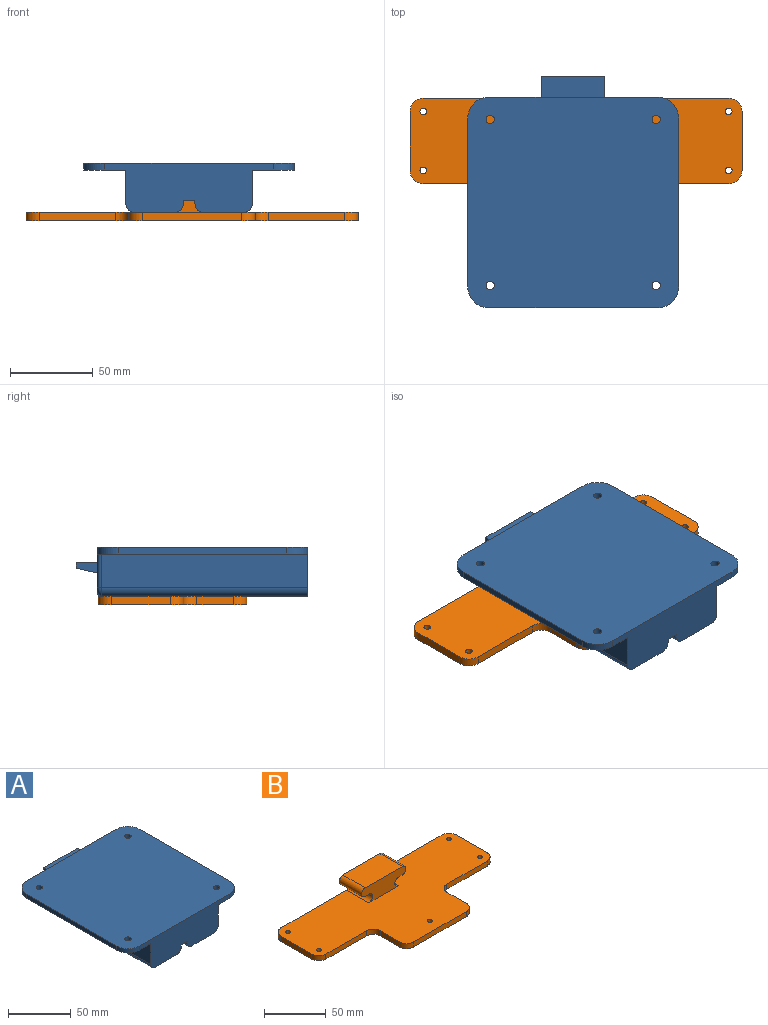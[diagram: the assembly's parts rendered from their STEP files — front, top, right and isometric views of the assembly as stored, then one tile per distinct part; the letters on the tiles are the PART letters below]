
ASSEMBLY  parts=2 mates=1
PART A: 55 faces, bbox 127x139.7x29.8 mm
  f0: plane 38.1x25.4mm, normal (0,0,-1), area 967.7mm2, adj f3,f27,f29,f33
  f1: plane 124.46x24.44mm, normal (0,0,-1), area 2850.8mm2, adj f2,f3,f9,f40,f42,f46
  f2: plane 101.6x29.4mm, normal (0,-1,0), area 2270.7mm2, adj f1,f10,f11,f12,f13,f15,f17,f23
  f3: plane 51.31x25.4mm, normal (0,1,0), area 840.4mm2, adj f0,f1,f4,f5,f6,f7,f8,f9
  f4: cylinder r=3.98mm len=22.86mm, axis (0,1,0), area 285.8mm2, adj f3,f5,f11,f51
  f5: plane 22.86x4.23mm, normal (0,0,1), area 96.8mm2, adj f3,f4,f6,f50
  f6: cylinder r=4.49mm len=22.86mm, axis (0,1,0), area 322.3mm2, adj f3,f5,f30,f49
  f7: cylinder r=4.49mm len=22.86mm, axis (0,1,0), area 322.3mm2, adj f3,f8,f26,f43
  f8: plane 22.86x4.23mm, normal (0,0,1), area 96.8mm2, adj f3,f7,f9,f44
  f9: cylinder r=3.98mm len=22.86mm, axis (0,1,0), area 285.8mm2, adj f1,f3,f8,f45
  f10: plane 124.46x20.32mm, normal (-1,0,0), area 2529mm2, adj f2,f17,f41,f54
  f11: plane 124.46x24.44mm, normal (0,0,-1), area 2850.8mm2, adj f2,f3,f4,f39,f41,f52
  f12: plane 124.46x20.32mm, normal (1,0,0), area 2529mm2, adj f2,f13,f42,f48
  f13: plane 127x27.94mm, normal (0,0,-1), area 3118.7mm2, adj f2,f12,f14,f18,f21,f22,f36,f38
  f14: plane 101.6x4mm, normal (1,0,0), area 406.4mm2, adj f13,f15,f36,f38
  f15: plane 127x127mm, normal (0,0,1), area 15912mm2, adj f2,f14,f16,f18,f19,f20,f21,f22
  f16: plane 101.6x4mm, normal (-1,0,0), area 406.4mm2, adj f15,f17,f35,f37
  f17: plane 127x27.94mm, normal (0,0,-1), area 3118.7mm2, adj f2,f10,f16,f18,f19,f20,f35,f37
  f18: plane 101.6x26.86mm, normal (0,1,0), area 937.4mm2, adj f13,f15,f17,f26,f30,f31,f35,f36
  f19: cylinder r=2.5mm len=5mm, axis (0,0,1), area 62.8mm2, adj f15,f17
  f20: cylinder r=2.5mm len=5mm, axis (0,0,1), area 62.8mm2, adj f15,f17
  f21: cylinder r=2.5mm len=5mm, axis (0,0,1), area 62.8mm2, adj f13,f15
  f22: cylinder r=2.5mm len=5mm, axis (0,0,1), area 62.8mm2, adj f13,f15
  f23: plane 101.6x1.92mm, normal (1,0,0), area 195.1mm2, adj f2,f3,f25,f39
  f24: plane 101.6x1.92mm, normal (-1,0,0), area 195.1mm2, adj f2,f3,f25,f40
  f25: plane 101.6x7mm, normal (0,0,-1), area 711.2mm2, adj f2,f3,f23,f24
  f26: plane 25.4x8.47mm, normal (-1,0,0), area 213.7mm2, adj f3,f7,f18,f31,f43
  f27: plane 38.1x6.21mm, normal (1,0,0), area 140.2mm2, adj f0,f3,f28,f32,f33,f34
  f28: plane 38.1x38.1mm, normal (0,0,1), area 1451.6mm2, adj f3,f27,f29,f32
  f29: plane 38.1x6.21mm, normal (-1,0,0), area 140.2mm2, adj f0,f3,f28,f32,f33,f34
  f30: plane 25.4x8.47mm, normal (1,0,0), area 213.7mm2, adj f3,f6,f18,f31,f49
  f31: plane 42.33x25.4mm, normal (0,0,-1), area 1075.3mm2, adj f3,f18,f26,f30
  f32: plane 38.1x3.18mm, normal (0,1,0), area 121mm2, adj f27,f28,f29,f34
  f33: plane 38.1x3.03mm, normal (0,-1,0), area 115.6mm2, adj f0,f27,f29,f34
  f34: plane 38.1x12.7mm, normal (0,0.23,-0.97), area 497.5mm2, adj f27,f29,f32,f33
  f35: cylinder r=12.7mm len=12.7mm, axis (0,0,-1), area 79.8mm2, adj f15,f16,f17,f18
  f36: cylinder r=12.7mm len=12.7mm, axis (0,0,1), area 79.8mm2, adj f13,f14,f15,f18
  f37: cylinder r=12.7mm len=12.7mm, axis (0,0,1), area 79.8mm2, adj f2,f15,f16,f17
  f38: cylinder r=12.7mm len=12.7mm, axis (0,0,-1), area 79.8mm2, adj f2,f13,f14,f15
  f39: cylinder r=5.08mm len=101.6mm, axis (0,1,0), area 810.7mm2, adj f2,f3,f11,f23
  f40: cylinder r=5.08mm len=101.6mm, axis (0,-1,0), area 810.7mm2, adj f1,f2,f3,f24
  f41: cylinder r=5.08mm len=124.46mm, axis (0,-1,0), area 993.1mm2, adj f2,f10,f11,f53
  f42: cylinder r=5.08mm len=124.46mm, axis (0,1,0), area 993.1mm2, adj f1,f2,f12,f47
  f43: torus R=7.03mm, axis (0,-1,0), area 67.8mm2, adj f7,f18,f26,f44
  f44: cylinder r=2.54mm len=4.23mm, axis (-1,0,0), area 16.9mm2, adj f8,f18,f43,f45
  f45: torus R=1.44mm, axis (0,-1,0), area 38.3mm2, adj f9,f18,f44,f46
  f46: cylinder r=2.54mm len=16.09mm, axis (1,0,0), area 64.2mm2, adj f1,f18,f45,f47
  f47: torus R=2.54mm, axis (0,-1,0), area 26.1mm2, adj f18,f42,f46,f48
  f48: cylinder r=2.54mm len=20.32mm, axis (0,0,1), area 81.1mm2, adj f12,f13,f18,f47
  f49: torus R=7.03mm, axis (0,-1,0), area 67.8mm2, adj f6,f18,f30,f50
  f50: cylinder r=2.54mm len=4.23mm, axis (-1,0,0), area 16.9mm2, adj f5,f18,f49,f51
  f51: torus R=1.44mm, axis (0,-1,0), area 38.3mm2, adj f4,f18,f50,f52
  f52: cylinder r=2.54mm len=16.09mm, axis (-1,0,0), area 64.2mm2, adj f11,f18,f51,f53
  f53: torus R=2.54mm, axis (0,-1,0), area 26.1mm2, adj f18,f41,f52,f54
  f54: cylinder r=2.54mm len=20.32mm, axis (0,0,-1), area 81.1mm2, adj f10,f17,f18,f53
PART B: 31 faces, bbox 200x89.6x21.9 mm
  f0: plane 35.5x5mm, normal (1,0,0), area 177.5mm2, adj f1,f20,f21,f22
  f1: cylinder r=8mm len=8mm, axis (0,0,-1), area 62.8mm2, adj f0,f2,f21,f22
  f2: plane 184x21.93mm, normal (0,1,0), area 1565.2mm2, adj f1,f3,f21,f22,f23,f24,f25,f26
  f3: cylinder r=8mm len=8mm, axis (0,0,-1), area 62.8mm2, adj f2,f4,f21,f22
  f4: plane 35.5x5mm, normal (-1,0,0), area 177.5mm2, adj f3,f5,f21,f22
  f5: cylinder r=8mm len=8mm, axis (0,0,-1), area 62.8mm2, adj f4,f6,f21,f22
  f6: plane 45.9x5mm, normal (0,-1,0), area 229.5mm2, adj f5,f7,f21,f22
  f7: cylinder r=8mm len=8mm, axis (0,0,-1), area 62.8mm2, adj f6,f8,f21,f22
  f8: plane 22.1x5mm, normal (-1,0,0), area 110.5mm2, adj f7,f9,f21,f22
  f9: cylinder r=8mm len=8mm, axis (0,0,-1), area 62.8mm2, adj f8,f10,f21,f22
  f10: plane 60.2x5mm, normal (0,-1,0), area 301mm2, adj f9,f11,f21,f22
  f11: cylinder r=8mm len=8mm, axis (0,0,-1), area 62.8mm2, adj f10,f12,f21,f22
  f12: plane 22.1x5mm, normal (1,0,0), area 110.5mm2, adj f11,f13,f21,f22
  f13: cylinder r=8mm len=8mm, axis (0,0,-1), area 62.8mm2, adj f12,f14,f21,f22
  f14: plane 45.9x5mm, normal (0,-1,0), area 229.5mm2, adj f13,f20,f21,f22
  f15: cylinder r=2mm len=5mm, axis (0,0,-1), area 62.8mm2, adj f21,f22
  f16: cylinder r=2mm len=5mm, axis (0,0,-1), area 62.8mm2, adj f21,f22
  f17: cylinder r=2mm len=5mm, axis (0,0,-1), area 62.8mm2, adj f21,f22
  f18: cylinder r=2mm len=5mm, axis (0,0,-1), area 62.8mm2, adj f21,f22
  f19: cylinder r=2mm len=5mm, axis (0,0,-1), area 62.8mm2, adj f21,f22
  f20: cylinder r=8mm len=8mm, axis (0,0,-1), area 62.8mm2, adj f0,f14,f21,f22
  f21: plane 200x89.6mm, normal (0,0,1), area 12225.2mm2, adj f0,f1,f2,f3,f4,f5,f6,f7
  f22: plane 200x89.6mm, normal (0,0,-1), area 13085.5mm2, adj f0,f1,f2,f3,f4,f5,f6,f7
  f23: cylinder r=4.23mm len=25.4mm, axis (0,1,0), area 337.8mm2, adj f2,f21,f29,f30
  f24: cylinder r=4.23mm len=25.4mm, axis (0,1,0), area 337.8mm2, adj f2,f21,f25,f30
  f25: plane 25.4x4.23mm, normal (0,0,-1), area 107.5mm2, adj f2,f24,f26,f30
  f26: cylinder r=4.23mm len=25.4mm, axis (0,1,0), area 337.8mm2, adj f2,f25,f27,f30
  f27: plane 42.33x25.4mm, normal (0,0,1), area 1075.3mm2, adj f2,f26,f28,f30
  f28: cylinder r=4.23mm len=25.4mm, axis (0,1,0), area 337.8mm2, adj f2,f27,f29,f30
  f29: plane 25.4x4.23mm, normal (0,0,-1), area 107.5mm2, adj f2,f23,f28,f30
  f30: plane 50.8x16.93mm, normal (0,-1,0), area 645.2mm2, adj f21,f23,f24,f25,f26,f27,f28,f29
PLACE A t=(-106.53,70.5,-3.17)mm
PLACE B t=(-104.81,-8.11,-14.56)mm
MATE planar B.f21 <-> A.f11  axis (0,0,1) through (-104.81,32.72,-9.56)mm
